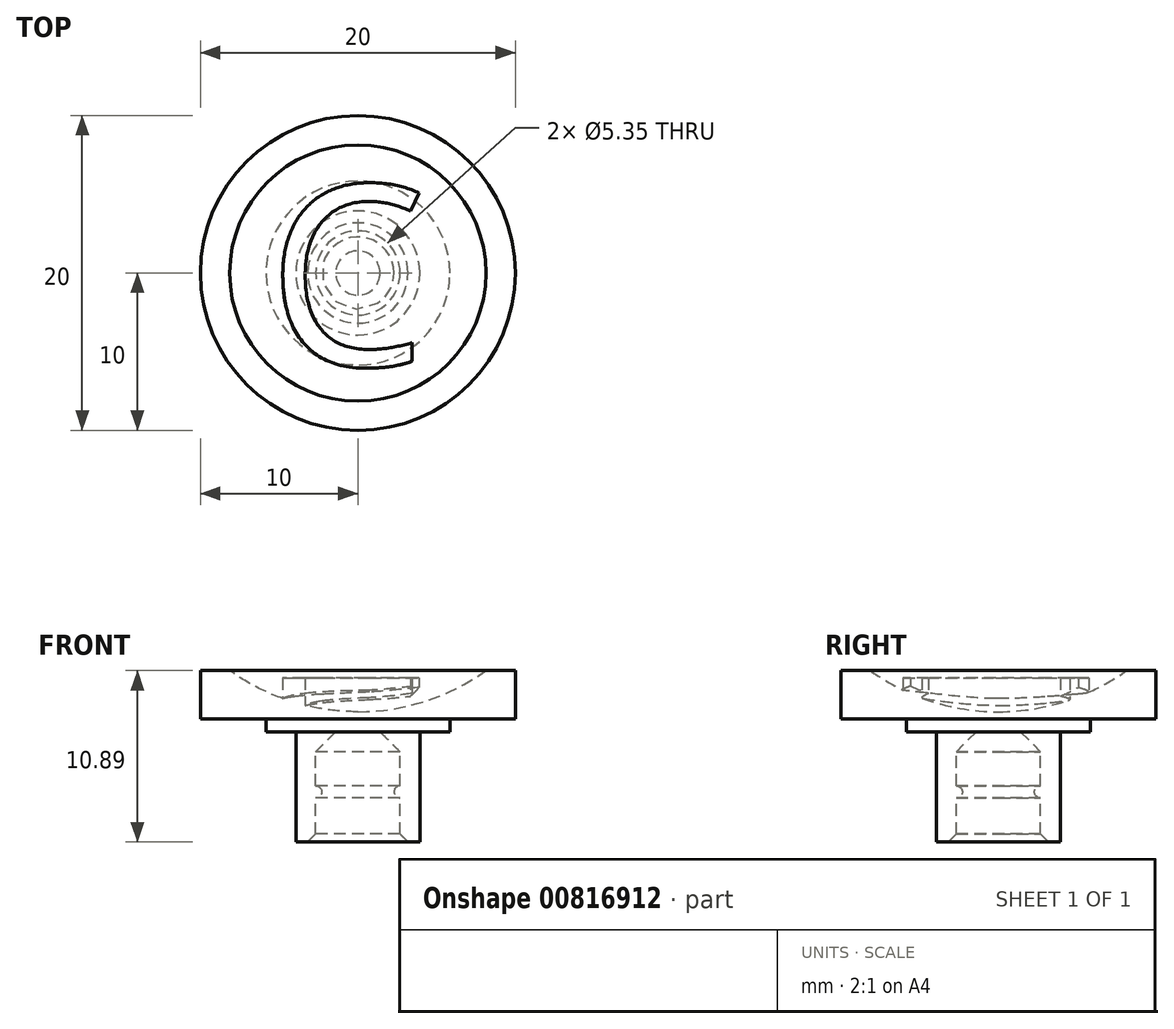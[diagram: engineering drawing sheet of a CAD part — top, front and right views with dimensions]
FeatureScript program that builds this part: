
annotation { "Feature Type Name" : "Feature", "Feature Type Description" : "" }
export const myFeature = defineFeature(function(context is Context, id is Id, definition is map)
    precondition{}
    {
        {
            var Q0;
            Q0=qCreatedBy(makeId("Front.planeOp"),FACE);
            var sketch = newSketch(context, id + "F0", { "sketchPlane" : qUnion([Q0])});
            skLineSegment(sketch, "E0", {"start": v(2.68, 0) * mm, "end": v(2.68, -3.44) * mm});
            skLineSegment(sketch, "E1", {"start": v(2.68, -7) * mm, "end": v(3.94, -7) * mm});
            skLineSegment(sketch, "E2", {"start": v(3.94, -7) * mm, "end": v(3.94, 0) * mm});
            skLineSegment(sketch, "E3", {"start": v(3.94, 0) * mm, "end": v(10, 0) * mm});
            skLineSegment(sketch, "E4", {"start": v(10, 0) * mm, "end": v(10, 5.48) * mm});
            skArc(sketch, "E5", {"start": v(0, 1.27) * mm, "mid": v(5.43, 2.37) * mm, "end": v(10, 5.48) * mm});
            skLineSegment(sketch, "E6", {"start": v(0, 1.27) * mm, "end": v(0, 0) * mm});
            skLineSegment(sketch, "E7", {"start": v(0, 0) * mm, "end": v(2.68, 0) * mm});
            skArc(sketch, "E8", {"start": v(2.68, -3.44) * mm, "mid": v(2.3, -3.82) * mm, "end": v(2.68, -4.2) * mm});
            skLineSegment(sketch, "E9.trimOffspring", {"start": v(2.68, -4.2) * mm, "end": v(2.68, -7) * mm});
            skSolve(sketch);
        }
        {
            var Q0;
            Q0=qSketchRegion(id+"F0",true);
            var Q1;
            Q1=sQuery(id+"F0.wireOp",EDGE,"E6");
            revolve(context, id + "F1", {"surfaceOperationType" : NewSurfaceOperationType.NEW, "entities" : qUnion([Q0]), "axis" : qUnion([Q1]), "revolveType" : RevolveType.FULL});
        }
        {
            var Q0;
            Q0=qCreatedBy(makeId("Top.planeOp"),FACE);
            var sketch = newSketch(context, id + "F2", { "sketchPlane" : qUnion([Q0])});
            skText(sketch, "E10", { "text": "C", "fontName": "OpenSans-Regular.ttf"});
            const initialGuessF2  = {"E10": [-0.00575, -0.00589, 1, 0, 0.01156]};
            skSetInitialGuess(sketch, initialGuessF2);
            skSolve(sketch);
        }
        {
            var Q0;
            Q0=qSketchRegion(id+"F2",true);
            extrude(context, id + "F3", {"entities" : qUnion([Q0]), "operationType" : NewBodyOperationType.ADD, "depth" : 3.4 * mm, "offsetDistance" : 25.4 * mm});
        }
        {
            var Q0;
            Q0=qCreatedBy(makeId("Right.planeOp"),FACE);
            var sketch = newSketch(context, id + "F4", { "sketchPlane" : qUnion([Q0])});
            skLineSegment(sketch, "E11.bottom", {"start": v(-17.16, 8.69) * mm, "end": v(19.43, 8.69) * mm});
            skLineSegment(sketch, "E11.top", {"start": v(-17.16, 3.89) * mm, "end": v(19.43, 3.89) * mm});
            skLineSegment(sketch, "E11.left", {"start": v(-17.16, 8.69) * mm, "end": v(-17.16, 3.89) * mm});
            skLineSegment(sketch, "E11.right", {"start": v(19.43, 8.69) * mm, "end": v(19.43, 3.89) * mm});
            skSolve(sketch);
        }
        {
            var Q0;
            Q0=qSketchRegion(id+"F4",true);
            extrude(context, id + "F5", {"entities" : qUnion([Q0]), "operationType" : NewBodyOperationType.REMOVE, "endBound" : BoundingType.SYMMETRIC, "depth" : 25.4 * mm, "offsetDistance" : 25.4 * mm});
        }
        {
            var Q0;
            Q0=makeQuery(id+"F1.opRevolve","SWEPT_EDGE",EDGE,{"disambiguationData":[OSD([sQuery(id+"F0.wireOp",EDGE,"E0"),sQuery(id+"F0.wireOp",EDGE,"E7")])]});
            chamfer(context, id + "F6", {"entities" : qUnion([Q0]), "width" : 1.27 * mm, "tangentPropagation" : true});
        }
        {
            var Q0;
            Q0=makeQuery(id+"F1.opRevolve","SWEPT_FACE",FACE,{"disambiguationData":[OSD([sQuery(id+"F0.wireOp",EDGE,"E3")])]});
            var sketch = newSketch(context, id + "F7", { "sketchPlane" : qUnion([Q0])});
            skCircle(sketch, "E12", {"center": v(0, 0) * mm, "radius": 5.84 * mm});
            skCircle(sketch, "E13", {"center": v(0, -0.88) * mm, "radius": 18.96 * mm});
            skSolve(sketch);
        }
        {
            var Q0;
            Q0 = qSketchRegion(id + "F7", true);
            extrude(context, id + "F8", {"entities" : qUnion([Q0]), "operationType" : NewBodyOperationType.REMOVE, "oppositeDirection" : true, "depth" : .8 * mm, "offsetDistance" : 25.4 * mm});
        }
        {
            var Q0;
            Q0=makeQuery(id+"F1.opRevolve","SWEPT_EDGE",EDGE,{"disambiguationData":[OSD([sQuery(id+"F0.wireOp",EDGE,"E1"),sQuery(id+"F0.wireOp",EDGE,"E9.trimOffspring")])]});
            chamfer(context, id + "F9", {"entities" : qUnion([Q0]), "width" : 0.5 * mm, "tangentPropagation" : true});
        }
    });
